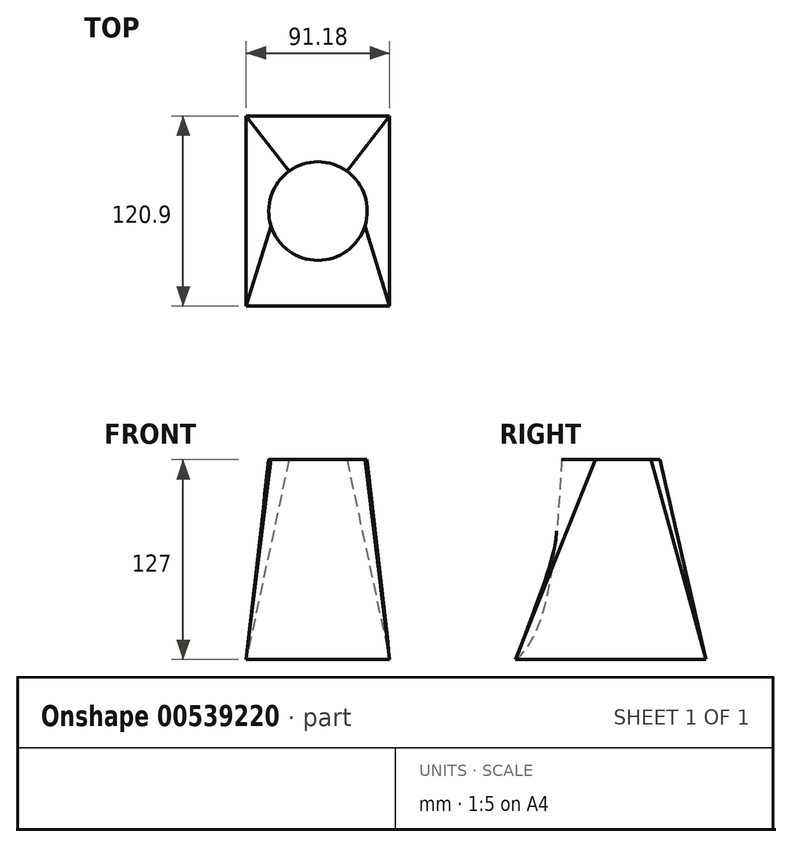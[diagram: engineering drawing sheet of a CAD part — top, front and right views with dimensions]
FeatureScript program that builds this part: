
annotation { "Feature Type Name" : "Feature", "Feature Type Description" : "" }
export const myFeature = defineFeature(function(context is Context, id is Id, definition is map)
    precondition{}
    {
        {
            var Q0;
            Q0=qCreatedBy(makeId("Top.planeOp"),FACE);
            var sketch = newSketch(context, id + "F0", { "sketchPlane" : qUnion([Q0])});
            skLineSegment(sketch, "E0.bottom", {"start": v(45.59, 60.45) * mm, "end": v(-45.59, 60.45) * mm});
            skLineSegment(sketch, "E0.top", {"start": v(45.59, -60.45) * mm, "end": v(-45.59, -60.45) * mm});
            skLineSegment(sketch, "E0.left", {"start": v(45.59, 60.45) * mm, "end": v(45.59, -60.45) * mm});
            skLineSegment(sketch, "E0.right", {"start": v(-45.59, 60.45) * mm, "end": v(-45.59, -60.45) * mm});
            skPoint(sketch, "E0.middle", {"position": v(0, 0) * mm});
            skSolve(sketch);
        }
        {
            var Q0;
            Q0=qCreatedBy(makeId("Top.planeOp"),FACE);
            cPlane(context, id + "F1", {"entities" : qUnion([Q0]), "cplaneType" : CPlaneType.OFFSET, "offset" : 127 * mm, "width" : 152.4 * mm, "height" : 152.4 * mm});
        }
        {
            var Q0;
            Q0=qCreatedBy(id+"F1.planeOp",FACE);
            var sketch = newSketch(context, id + "F2", { "sketchPlane" : qUnion([Q0])});
            skPoint(sketch, "E1.middle", {"position": v(0, 0) * mm});
            skCircle(sketch, "E2", {"center": v(0, 0) * mm, "radius": 31.3 * mm});
            skSolve(sketch);
        }
        {
            var Q0;
            Q0=qCreatedBy(makeId("Right.planeOp"),FACE);
            var sketch = newSketch(context, id + "F3", { "sketchPlane" : qUnion([Q0])});
            skLineSegment(sketch, "E3.0", {"start": v(-31.3, 127) * mm, "end": v(31.3, 127) * mm});
            skLineSegment(sketch, "E4.0", {"start": v(60.45, 0) * mm, "end": v(-60.45, 0) * mm});
            skFitSpline(sketch, "E5", {"points": [v(-31.3, 127) * mm, v(-60.45, 0) * mm, v(-134.8, 0) * mm], "startDerivative": vector(-16.52, -286.43) * mm, "endDerivative": vector(-198.94, 47.97) * mm});
            skSolve(sketch);
        }
        {
            var Q0;
            Q0=makeQuery(id+"F2.imprint","IMPRINT",FACE,{"disambiguationData":[TD([[makeQuery(id+"F2.imprint","IMPRINT",EDGE,{"derivedFrom":sQuery(id+"F2.wireOp",EDGE,"E2")}),1.0]])]});
            var Q1;
            Q1=makeQuery(id+"F0.imprint","IMPRINT",FACE,{"disambiguationData":[TD([[makeQuery(id+"F0.imprint","IMPRINT",EDGE,{"derivedFrom":sQuery(id+"F0.wireOp",EDGE,"E0.bottom")}),1.0]])]});
            var Q2;
            Q2=sQuery(id+"F3.wireOp",EDGE,"E5");
            loft(context, id + "F4", {"addGuides" : true, "sheetProfilesArray" : [{ "sheetProfileEntities" : qUnion([Q0]) }, { "sheetProfileEntities" : qUnion([Q1]) }], "guidesArray" : [{ "guideEntities" : qUnion([Q2]), "guideDerivativeType" : LoftGuideDerivativeType.DEFAULT, "guideDerivativeMagnitude" : 1 }]});
        }
    });
